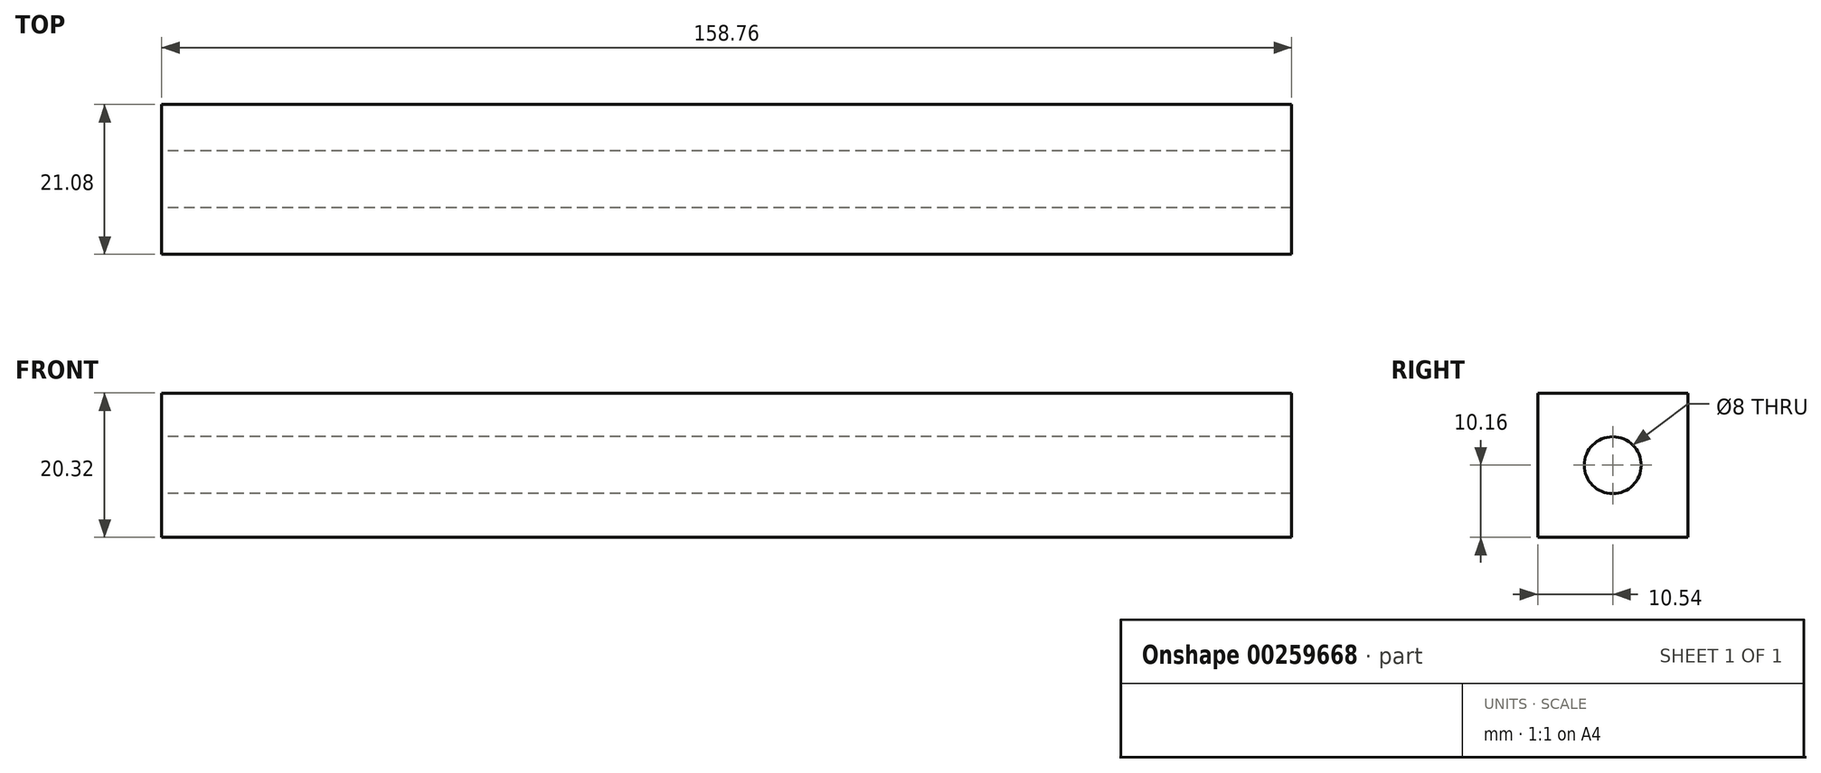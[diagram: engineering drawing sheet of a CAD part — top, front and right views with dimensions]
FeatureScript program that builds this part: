
annotation { "Feature Type Name" : "Feature", "Feature Type Description" : "" }
export const myFeature = defineFeature(function(context is Context, id is Id, definition is map)
    precondition{}
    {
        {
            var Q0;
            Q0=qCreatedBy(makeId("Right.planeOp"),FACE);
            var sketch = newSketch(context, id + "F0", { "sketchPlane" : qUnion([Q0])});
            skLineSegment(sketch, "E0.bottom", {"start": v(10.54, 10.16) * mm, "end": v(-10.54, 10.16) * mm});
            skLineSegment(sketch, "E0.top", {"start": v(10.54, -10.16) * mm, "end": v(-10.54, -10.16) * mm});
            skLineSegment(sketch, "E0.left", {"start": v(10.54, 10.16) * mm, "end": v(10.54, -10.16) * mm});
            skLineSegment(sketch, "E0.right", {"start": v(-10.54, 10.16) * mm, "end": v(-10.54, -10.16) * mm});
            skPoint(sketch, "E0.middle", {"position": v(0, 0) * mm});
            skCircle(sketch, "E1", {"center": v(0, 0) * mm, "radius": 4 * mm});
            skSolve(sketch);
        }
        {
            var Q0;
            Q0 = qSketchRegion(id + "F0", true);
            extrude(context, id + "F1", {"entities" : qUnion([Q0]), "endBound" : BoundingType.SYMMETRIC, "depth" : 158.75 * mm});
        }
    });
